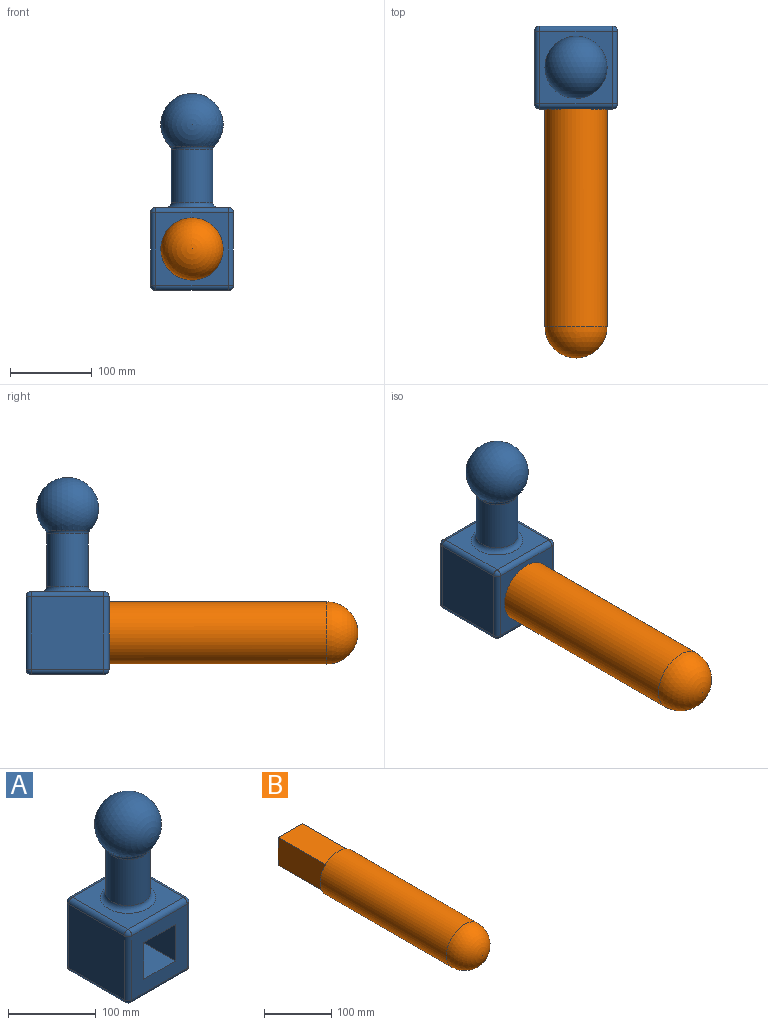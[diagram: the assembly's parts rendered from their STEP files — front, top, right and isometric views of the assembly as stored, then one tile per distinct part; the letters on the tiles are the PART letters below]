
ASSEMBLY  parts=2 mates=1
PART A: 34 faces, bbox 101.6x101.6x241.3 mm
  f0: plane 88.9x88.9mm, normal (0,-1,0), area 5322.6mm2, adj f8,f9,f10,f11,f22,f27,f30,f33
  f1: plane 88.9x88.9mm, normal (1,0,0), area 7903.2mm2, adj f19,f28,f29,f33
  f2: plane 88.9x88.9mm, normal (0,1,0), area 5322.6mm2, adj f8,f9,f10,f11,f14,f18,f19,f20
  f3: plane 88.9x88.9mm, normal (-1,0,0), area 7903.2mm2, adj f14,f17,f21,f22
  f4: plane 88.9x88.9mm, normal (0,0,1), area 4736.3mm2, adj f13,f17,f18,f27,f28
  f5: plane 88.9x88.9mm, normal (0,0,-1), area 7903.2mm2, adj f20,f21,f29,f30
  f6: cylinder r=25.4mm len=64.14mm, axis (0,0,-1), area 10236.5mm2, adj f12,f13
  f7: sphere r=38.1mm, area 15504.5mm2, adj f12
  f8: plane 101.6x50.8mm, normal (-1,0,0), area 5161.3mm2, adj f0,f2,f9,f11
  f9: plane 101.6x50.8mm, normal (0,0,-1), area 5161.3mm2, adj f0,f2,f8,f10
  f10: plane 101.6x50.8mm, normal (1,0,0), area 5161.3mm2, adj f0,f2,f9,f11
  f11: plane 101.6x50.8mm, normal (0,0,1), area 5161.3mm2, adj f0,f2,f8,f10
  f12: torus R=31.75mm, axis (0,0,1), area 804.7mm2, adj f6,f7
  f13: torus R=31.75mm, axis (0,0,1), area 1736.5mm2, adj f4,f6
  f14: cylinder r=6.35mm len=88.9mm, axis (0,0,-1), area 886.7mm2, adj f2,f3,f15,f16
  f15: sphere r=6.35mm, area 63.3mm2, adj f14,f17,f18
  f16: sphere r=6.35mm, area 63.3mm2, adj f14,f20,f21
  f17: cylinder r=6.35mm len=88.9mm, axis (0,1,0), area 886.7mm2, adj f3,f4,f15,f23
  f18: cylinder r=6.35mm len=88.9mm, axis (1,0,0), area 886.7mm2, adj f2,f4,f15,f24
  f19: cylinder r=6.35mm len=88.9mm, axis (0,0,1), area 886.7mm2, adj f1,f2,f24,f25
  f20: cylinder r=6.35mm len=88.9mm, axis (-1,0,0), area 886.7mm2, adj f2,f5,f16,f25
  f21: cylinder r=6.35mm len=88.9mm, axis (0,-1,0), area 886.7mm2, adj f3,f5,f16,f26
  f22: cylinder r=6.35mm len=88.9mm, axis (0,0,1), area 886.7mm2, adj f0,f3,f23,f26
  f23: sphere r=6.35mm, area 63.3mm2, adj f17,f22,f27
  f24: sphere r=6.35mm, area 63.3mm2, adj f18,f19,f28
  f25: sphere r=6.35mm, area 63.3mm2, adj f19,f20,f29
  f26: sphere r=6.35mm, area 63.3mm2, adj f21,f22,f30
  f27: cylinder r=6.35mm len=88.9mm, axis (-1,0,0), area 886.7mm2, adj f0,f4,f23,f31
  f28: cylinder r=6.35mm len=88.9mm, axis (0,-1,0), area 886.7mm2, adj f1,f4,f24,f31
  f29: cylinder r=6.35mm len=88.9mm, axis (0,1,0), area 886.7mm2, adj f1,f5,f25,f32
  f30: cylinder r=6.35mm len=88.9mm, axis (1,0,0), area 886.7mm2, adj f0,f5,f26,f32
  f31: sphere r=6.35mm, area 63.3mm2, adj f27,f28,f33
  f32: sphere r=6.35mm, area 63.3mm2, adj f29,f30,f33
  f33: cylinder r=6.35mm len=88.9mm, axis (0,0,-1), area 886.7mm2, adj f0,f1,f31,f32
PART B: 8 faces, bbox 76.2x406.4x76.2 mm
  f0: plane 101.6x50.8mm, normal (1,0,0), area 5161.3mm2, adj f1,f3,f4,f5
  f1: plane 101.6x50.8mm, normal (0,0,1), area 5161.3mm2, adj f0,f2,f4,f5
  f2: plane 101.6x50.8mm, normal (-1,0,0), area 5161.3mm2, adj f1,f3,f4,f5
  f3: plane 101.6x50.8mm, normal (0,0,-1), area 5161.3mm2, adj f0,f2,f4,f5
  f4: plane 50.8x50.8mm, normal (0,1,0), area 2580.6mm2, adj f0,f1,f2,f3
  f5: plane 76.2x76.2mm, normal (0,1,0), area 1979.7mm2, adj f0,f1,f2,f3,f6
  f6: cylinder r=38.1mm len=266.7mm, axis (0,1,0), area 63845.1mm2, adj f5,f7
  f7: sphere r=38.1mm, area 9120.7mm2, adj f6
PLACE A t=(32.4,164.91,62.63)mm fixed
PLACE B t=(32.4,215.71,113.43)mm
MATE fastened B.f6 <-> A.f2  axis (0,1,0) through (32.4,215.71,113.43)mm
